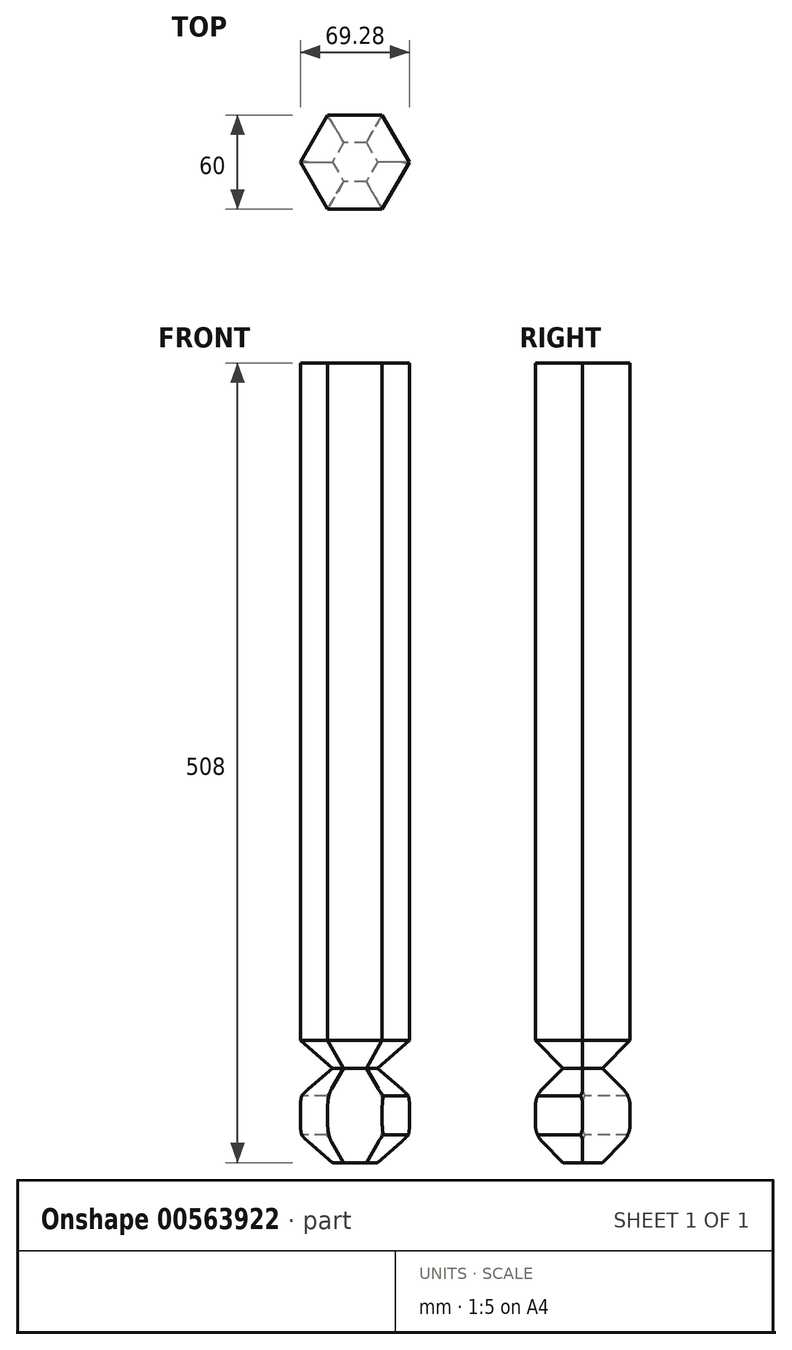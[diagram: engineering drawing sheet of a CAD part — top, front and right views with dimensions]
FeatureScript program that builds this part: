
annotation { "Feature Type Name" : "Feature", "Feature Type Description" : "" }
export const myFeature = defineFeature(function(context is Context, id is Id, definition is map)
    precondition{}
    {
        {
            var Q0;
            Q0=qCreatedBy(makeId("Top.planeOp"),FACE);
            var sketch = newSketch(context, id + "F0", { "sketchPlane" : qUnion([Q0])});
            skCircle(sketch, "E0.cCircle", {"center": v(0, 0) * mm, "radius": 30 * mm, "construction": true});
            skLineSegment(sketch, "E0.0", {"start": v(-17.32, 30) * mm, "end": v(17.32, 30) * mm});
            skLineSegment(sketch, "E0.1", {"start": v(17.32, 30) * mm, "end": v(34.64, 0) * mm});
            skLineSegment(sketch, "E0.2", {"start": v(34.64, 0) * mm, "end": v(17.32, -30) * mm});
            skLineSegment(sketch, "E0.3", {"start": v(17.32, -30) * mm, "end": v(-17.32, -30) * mm});
            skLineSegment(sketch, "E0.4", {"start": v(-17.32, -30) * mm, "end": v(-34.64, 0) * mm});
            skLineSegment(sketch, "E0.5", {"start": v(-34.64, 0) * mm, "end": v(-17.32, 30) * mm});
            skPoint(sketch, "E0.0.midPoint", {"position": v(0, 30) * mm});
            skSolve(sketch);
        }
        {
            var Q0;
            Q0=makeQuery(id+"F0.imprint","IMPRINT",FACE,{"disambiguationData":[TD([[makeQuery(id+"F0.imprint","IMPRINT",EDGE,{"derivedFrom":sQuery(id+"F0.wireOp",EDGE,"E0.0")}),-1.0]])]});
            extrude(context, id + "F1", {"entities" : qUnion([Q0]), "depth" : 508 * mm, "offsetDistance" : 25.4 * mm});
        }
        {
            var Q0;
            Q0=makeQuery(id+"F1.opExtrude","CAP_VERTEX",VERTEX,{"disambiguationData":[OSD([sQuery(id+"F0.wireOp",EDGE,"E0.2"),sQuery(id+"F0.wireOp",EDGE,"E0.3")])],"isStart":true});
            var Q1;
            Q1=makeQuery(id+"F1.opExtrude","CAP_VERTEX",VERTEX,{"disambiguationData":[OSD([sQuery(id+"F0.wireOp",EDGE,"E0.0"),sQuery(id+"F0.wireOp",EDGE,"E0.5")])],"isStart":true});
            cPlane(context, id + "F2", {"entities" : qUnion([Q0, Q1]), "cplaneType" : CPlaneType.MID_PLANE, "offset" : 25 * mm, "width" : 150 * mm, "height" : 150 * mm});
        }
        {
            var Q0;
            Q0=makeQuery(id+"F1.opExtrude","CAP_VERTEX",VERTEX,{"disambiguationData":[OSD([sQuery(id+"F0.wireOp",EDGE,"E0.3"),sQuery(id+"F0.wireOp",EDGE,"E0.4")])],"isStart":true});
            var Q1;
            Q1=makeQuery(id+"F1.opExtrude","CAP_VERTEX",VERTEX,{"disambiguationData":[OSD([sQuery(id+"F0.wireOp",EDGE,"E0.0"),sQuery(id+"F0.wireOp",EDGE,"E0.1")])],"isStart":true});
            cPlane(context, id + "F3", {"entities" : qUnion([Q0, Q1]), "cplaneType" : CPlaneType.MID_PLANE, "offset" : 25 * mm, "width" : 150 * mm, "height" : 150 * mm});
        }
        {
            var Q0;
            Q0=qCreatedBy(makeId("Right.planeOp"),FACE);
            var sketch = newSketch(context, id + "F4", { "sketchPlane" : qUnion([Q0])});
            skCircle(sketch, "E1.cCircle", {"center": v(0, 30) * mm, "radius": 30 * mm, "construction": true});
            skLineSegment(sketch, "E1.0", {"start": v(-12.43, 0) * mm, "end": v(12.43, 0) * mm});
            skLineSegment(sketch, "E1.1", {"start": v(-30, 17.57) * mm, "end": v(-12.43, 0) * mm});
            skLineSegment(sketch, "E1.2", {"start": v(-30, 42.43) * mm, "end": v(-30, 17.57) * mm});
            skLineSegment(sketch, "E1.3", {"start": v(-12.43, 60) * mm, "end": v(-30, 42.43) * mm});
            skLineSegment(sketch, "E1.4", {"start": v(12.43, 60) * mm, "end": v(-12.43, 60) * mm, "construction": true});
            skLineSegment(sketch, "E1.5", {"start": v(30, 42.43) * mm, "end": v(12.43, 60) * mm});
            skLineSegment(sketch, "E1.6", {"start": v(30, 17.57) * mm, "end": v(30, 42.43) * mm});
            skLineSegment(sketch, "E1.7", {"start": v(12.43, 0) * mm, "end": v(30, 17.57) * mm});
            skPoint(sketch, "E1.0.midPoint", {"position": v(0, 0) * mm});
            skLineSegment(sketch, "E2.MirrorCS", {"start": v(30, 77.57) * mm, "end": v(12.43, 60) * mm});
            skLineSegment(sketch, "E3.MirrorCS", {"start": v(-12.43, 60) * mm, "end": v(-30, 77.57) * mm});
            skLineSegment(sketch, "E4", {"start": v(30, 77.57) * mm, "end": v(30, -5) * mm});
            skLineSegment(sketch, "E5", {"start": v(30, -5) * mm, "end": v(-30, -5) * mm});
            skLineSegment(sketch, "E6", {"start": v(-30, -5) * mm, "end": v(-30, 77.57) * mm});
            skSolve(sketch);
        }
        {
            var Q0;
            Q0=qCreatedBy(id+"F2.planeOp",FACE);
            var sketch = newSketch(context, id + "F5", { "sketchPlane" : qUnion([Q0])});
            skCircle(sketch, "E7.cCircle", {"center": v(0, 30) * mm, "radius": 30 * mm, "construction": true});
            skLineSegment(sketch, "E7.0", {"start": v(-12.43, 0) * mm, "end": v(12.43, 0) * mm});
            skLineSegment(sketch, "E7.1", {"start": v(-30, 17.57) * mm, "end": v(-12.43, 0) * mm});
            skLineSegment(sketch, "E7.2", {"start": v(-30, 42.43) * mm, "end": v(-30, 17.57) * mm});
            skLineSegment(sketch, "E7.3", {"start": v(-12.43, 60) * mm, "end": v(-30, 42.43) * mm});
            skLineSegment(sketch, "E7.4", {"start": v(12.43, 60) * mm, "end": v(-12.43, 60) * mm, "construction": true});
            skLineSegment(sketch, "E7.5", {"start": v(30, 42.43) * mm, "end": v(12.43, 60) * mm});
            skLineSegment(sketch, "E7.6", {"start": v(30, 17.57) * mm, "end": v(30, 42.43) * mm});
            skLineSegment(sketch, "E7.7", {"start": v(12.43, 0) * mm, "end": v(30, 17.57) * mm});
            skPoint(sketch, "E7.0.midPoint", {"position": v(0, 0) * mm});
            skLineSegment(sketch, "E8.MirrorCS", {"start": v(30, 77.57) * mm, "end": v(12.43, 60) * mm});
            skLineSegment(sketch, "E9.MirrorCS", {"start": v(-12.43, 60) * mm, "end": v(-30, 77.57) * mm});
            skLineSegment(sketch, "E10", {"start": v(30, 77.57) * mm, "end": v(30, -5) * mm});
            skLineSegment(sketch, "E11", {"start": v(30, -5) * mm, "end": v(-30, -5) * mm});
            skLineSegment(sketch, "E12", {"start": v(-30, -5) * mm, "end": v(-30, 77.57) * mm});
            skSolve(sketch);
        }
        {
            var Q0;
            Q0=qCreatedBy(id+"F3.planeOp",FACE);
            var sketch = newSketch(context, id + "F6", { "sketchPlane" : qUnion([Q0])});
            skCircle(sketch, "E13.cCircle", {"center": v(0, 30) * mm, "radius": 30 * mm, "construction": true});
            skLineSegment(sketch, "E13.0", {"start": v(-12.43, 0) * mm, "end": v(12.43, 0) * mm});
            skLineSegment(sketch, "E13.1", {"start": v(-30, 17.57) * mm, "end": v(-12.43, 0) * mm});
            skLineSegment(sketch, "E13.2", {"start": v(-30, 42.43) * mm, "end": v(-30, 17.57) * mm});
            skLineSegment(sketch, "E13.3", {"start": v(-12.43, 60) * mm, "end": v(-30, 42.43) * mm});
            skLineSegment(sketch, "E13.4", {"start": v(12.43, 60) * mm, "end": v(-12.43, 60) * mm, "construction": true});
            skLineSegment(sketch, "E13.5", {"start": v(30, 42.43) * mm, "end": v(12.43, 60) * mm});
            skLineSegment(sketch, "E13.6", {"start": v(30, 17.57) * mm, "end": v(30, 42.43) * mm});
            skLineSegment(sketch, "E13.7", {"start": v(12.43, 0) * mm, "end": v(30, 17.57) * mm});
            skPoint(sketch, "E13.0.midPoint", {"position": v(0, 0) * mm});
            skLineSegment(sketch, "E14.MirrorCS", {"start": v(30, 77.57) * mm, "end": v(12.43, 60) * mm});
            skLineSegment(sketch, "E15.MirrorCS", {"start": v(-12.43, 60) * mm, "end": v(-30, 77.57) * mm});
            skLineSegment(sketch, "E16", {"start": v(30, 77.57) * mm, "end": v(30, -5) * mm});
            skLineSegment(sketch, "E17", {"start": v(30, -5) * mm, "end": v(-30, -5) * mm});
            skLineSegment(sketch, "E18", {"start": v(-30, -5) * mm, "end": v(-30, 77.57) * mm});
            skSolve(sketch);
        }
        {
            var Q0;
            Q0 = qSketchRegion(id + "F4", true);
            extrude(context, id + "F7", {"entities" : qUnion([Q0]), "operationType" : NewBodyOperationType.REMOVE, "endBound" : BoundingType.THROUGH_ALL, "depth" : 25 * mm, "offsetDistance" : 25 * mm, "hasSecondDirection" : true, "secondDirectionBound" : SecondDirectionBoundingType.THROUGH_ALL, "secondDirectionOppositeDirection" : true, "secondDirectionDepth" : 25 * mm});
        }
        {
            var Q0;
            Q0 = qSketchRegion(id + "F5", true);
            extrude(context, id + "F8", {"entities" : qUnion([Q0]), "operationType" : NewBodyOperationType.REMOVE, "endBound" : BoundingType.THROUGH_ALL, "depth" : 25 * mm, "offsetDistance" : 25 * mm, "hasSecondDirection" : true, "secondDirectionBound" : SecondDirectionBoundingType.THROUGH_ALL, "secondDirectionOppositeDirection" : true, "secondDirectionDepth" : 25 * mm});
        }
        {
            var Q0;
            Q0 = qSketchRegion(id + "F6", true);
            extrude(context, id + "F9", {"entities" : qUnion([Q0]), "operationType" : NewBodyOperationType.REMOVE, "endBound" : BoundingType.THROUGH_ALL, "depth" : 25 * mm, "offsetDistance" : 25 * mm, "hasSecondDirection" : true, "secondDirectionBound" : SecondDirectionBoundingType.THROUGH_ALL, "secondDirectionOppositeDirection" : true, "secondDirectionDepth" : 25 * mm});
        }
        {
            var Q0;
            Q0=makeQuery(id+"F8.boolean.opBoolean","COPY",EDGE,{"derivedFrom":makeQuery(id+"F8.opExtrude","SWEPT_EDGE",EDGE,{"disambiguationData":[OSD([sQuery(id+"F5.wireOp",EDGE,"E7.7"),sQuery(id+"F5.wireOp",EDGE,"E10")])]})});
            var Q1;
            Q1=makeQuery(id+"F7.boolean.opBoolean","COPY",EDGE,{"derivedFrom":makeQuery(id+"F7.opExtrude","SWEPT_EDGE",EDGE,{"disambiguationData":[OSD([sQuery(id+"F4.wireOp",EDGE,"E1.1"),sQuery(id+"F4.wireOp",EDGE,"E6")])]})});
            var Q2;
            Q2=makeQuery(id+"F9.boolean.opBoolean","COPY",EDGE,{"derivedFrom":makeQuery(id+"F9.opExtrude","SWEPT_EDGE",EDGE,{"disambiguationData":[OSD([sQuery(id+"F6.wireOp",EDGE,"E13.1"),sQuery(id+"F6.wireOp",EDGE,"E18")])]})});
            var Q3;
            Q3=makeQuery(id+"F8.boolean.opBoolean","COPY",EDGE,{"derivedFrom":makeQuery(id+"F8.opExtrude","SWEPT_EDGE",EDGE,{"disambiguationData":[OSD([sQuery(id+"F5.wireOp",EDGE,"E7.1"),sQuery(id+"F5.wireOp",EDGE,"E12")])]})});
            var Q4;
            Q4=makeQuery(id+"F7.boolean.opBoolean","COPY",EDGE,{"derivedFrom":makeQuery(id+"F7.opExtrude","SWEPT_EDGE",EDGE,{"disambiguationData":[OSD([sQuery(id+"F4.wireOp",EDGE,"E1.7"),sQuery(id+"F4.wireOp",EDGE,"E4")])]})});
            var Q5;
            Q5=makeQuery(id+"F9.boolean.opBoolean","COPY",EDGE,{"derivedFrom":makeQuery(id+"F9.opExtrude","SWEPT_EDGE",EDGE,{"disambiguationData":[OSD([sQuery(id+"F6.wireOp",EDGE,"E13.7"),sQuery(id+"F6.wireOp",EDGE,"E16")])]})});
            var Q6;
            Q6=makeQuery(id+"F8.boolean.opBoolean","COPY",EDGE,{"derivedFrom":makeQuery(id+"F8.opExtrude","SWEPT_EDGE",EDGE,{"disambiguationData":[OSD([sQuery(id+"F5.wireOp",EDGE,"E7.3"),sQuery(id+"F5.wireOp",EDGE,"E12")])]})});
            var Q7;
            Q7=makeQuery(id+"F9.boolean.opBoolean","COPY",EDGE,{"derivedFrom":makeQuery(id+"F9.opExtrude","SWEPT_EDGE",EDGE,{"disambiguationData":[OSD([sQuery(id+"F6.wireOp",EDGE,"E13.3"),sQuery(id+"F6.wireOp",EDGE,"E18")])]})});
            var Q8;
            Q8=makeQuery(id+"F7.boolean.opBoolean","COPY",EDGE,{"derivedFrom":makeQuery(id+"F7.opExtrude","SWEPT_EDGE",EDGE,{"disambiguationData":[OSD([sQuery(id+"F4.wireOp",EDGE,"E1.5"),sQuery(id+"F4.wireOp",EDGE,"E4")])]})});
            var Q9;
            Q9=makeQuery(id+"F9.boolean.opBoolean","COPY",EDGE,{"derivedFrom":makeQuery(id+"F9.opExtrude","SWEPT_EDGE",EDGE,{"disambiguationData":[OSD([sQuery(id+"F6.wireOp",EDGE,"E13.5"),sQuery(id+"F6.wireOp",EDGE,"E16")])]})});
            var Q10;
            Q10=makeQuery(id+"F7.boolean.opBoolean","COPY",EDGE,{"derivedFrom":makeQuery(id+"F7.opExtrude","SWEPT_EDGE",EDGE,{"disambiguationData":[OSD([sQuery(id+"F4.wireOp",EDGE,"E1.3"),sQuery(id+"F4.wireOp",EDGE,"E6")])]})});
            var Q11;
            Q11=makeQuery(id+"F8.boolean.opBoolean","COPY",EDGE,{"derivedFrom":makeQuery(id+"F8.opExtrude","SWEPT_EDGE",EDGE,{"disambiguationData":[OSD([sQuery(id+"F5.wireOp",EDGE,"E7.5"),sQuery(id+"F5.wireOp",EDGE,"E10")])]})});
            var Q12;
            Q12=makeQuery(id+"F7.boolean.opBoolean","COPY",EDGE,{"derivedFrom":makeQuery(id+"F7.opExtrude","SWEPT_EDGE",EDGE,{"disambiguationData":[OSD([sQuery(id+"F4.wireOp",EDGE,"E1.0"),sQuery(id+"F4.wireOp",EDGE,"E1.1")])]})});
            var Q13;
            Q13=makeQuery(id+"F9.boolean.opBoolean","COPY",EDGE,{"derivedFrom":makeQuery(id+"F9.opExtrude","SWEPT_EDGE",EDGE,{"disambiguationData":[OSD([sQuery(id+"F6.wireOp",EDGE,"E13.0"),sQuery(id+"F6.wireOp",EDGE,"E13.1")])]})});
            var Q14;
            Q14=makeQuery(id+"F8.boolean.opBoolean","COPY",EDGE,{"derivedFrom":makeQuery(id+"F8.opExtrude","SWEPT_EDGE",EDGE,{"disambiguationData":[OSD([sQuery(id+"F5.wireOp",EDGE,"E7.0"),sQuery(id+"F5.wireOp",EDGE,"E7.1")])]})});
            var Q15;
            Q15=makeQuery(id+"F7.boolean.opBoolean","COPY",EDGE,{"derivedFrom":makeQuery(id+"F7.opExtrude","SWEPT_EDGE",EDGE,{"disambiguationData":[OSD([sQuery(id+"F4.wireOp",EDGE,"E1.0"),sQuery(id+"F4.wireOp",EDGE,"E1.7")])]})});
            var Q16;
            Q16=makeQuery(id+"F9.boolean.opBoolean","COPY",EDGE,{"derivedFrom":makeQuery(id+"F9.opExtrude","SWEPT_EDGE",EDGE,{"disambiguationData":[OSD([sQuery(id+"F6.wireOp",EDGE,"E13.0"),sQuery(id+"F6.wireOp",EDGE,"E13.7")])]})});
            var Q17;
            Q17=makeQuery(id+"F8.boolean.opBoolean","COPY",EDGE,{"derivedFrom":makeQuery(id+"F8.opExtrude","SWEPT_EDGE",EDGE,{"disambiguationData":[OSD([sQuery(id+"F5.wireOp",EDGE,"E7.0"),sQuery(id+"F5.wireOp",EDGE,"E7.7")])]})});
            fillet(context, id + "F10", {"entities" : qUnion([Q0, Q1, Q2, Q3, Q4, Q5, Q6, Q7, Q8, Q9, Q10, Q11, Q12, Q13, Q14, Q15, Q16, Q17]), "radius" : 15 * mm, "tangentPropagation" : true, "allowEdgeOverflow" : false});
        }
    });
